# Revit family: Steni - Panel - Nature Type C
name_source: partatom
category: Generic Models
revit_build: Autodesk Revit Architecture 2014 (Build: 20131024_2115(x64)
units: mm (PartAtom-declared; Revit-internal decimal feet)

## types (3) — shared parameters
Allowable Variation = ± 2 mm
BIMobject Category = Cladding
BIMobject QR code url = http://steni.bimobject.com
Density = Apprx. 2000 Kg/m³
Design country = Norway
Diagonal Deviation = 3 mm
Drilling Distance Tolerance = ± 5 mm
Edge Straightness Full Size = 1 mm
Edition number = 1
Elasticity Module = 5000 MPa
Flexural Strength = 40 MPa
Hardness Of Aggregate = SEE SPEC.
Heat Conductivity = 0.55 W/m°C
Heat Resistance = 0.0074 m²°C/W
Humidity Altered Dimension = 5.2 X 106 m/m x%RF
IFC Classification = Covering
Impact Strength = 20 KJ / m 2
Impermeability = 100%
Installation instructions = http://steni.com
Manufacturer = Steni
Manufacturer URL = www.steni.com
Manufacturer country = Norway
Model = Steni - Panel - Nature Type C
Name of the object = Steni - Panel - Nature Type C
No Damage = 300 CYCLE
NominalHeight = 1195
NominalWidth = 3500
Penetration Of Water Vapour = 3,3 X 10-12 Kg/m²sPa
Product certification = http://steni.co.uk
Product data url = http://steni.com
Product family = Steni Nature
Product group = Coarse
Riverse Side = PLANE
Size Of Aggregate Particle = 5-8mm
Standard Length = 3500 mm
Standard Width = 1195 mm
Technical description = http://steni.no
Temperature Expansion (-20° +65°) = 0.021 mm/m°C
Tensile Strength = 15 N/mm²
Thickness 2 = Apprx. 14 ,mm
Type Of Aggregate = SEE SPEC.
UNSPC Category = Siding and exterior wall materials
UNSPC code = 301518
URL = http://steni.bimobject.com
Uniclass 1.4 Code = L381
Uniclass 1.4 Description = Facades and roofs
Water Absorbtion After 28 days = <1.5 %
Weight Net (kg) = Apprx. 18 Kg/m²

## per-type parameters (varying)
| type | Material main | Product SKU |
| SN 140 | Steni - Nature SN140 | SN140 |
| SN 117 | Steni - Nature SN117 | SN117 |
| SN 100 | Steni - Nature SN100 | SN100 |

## geometry (parser evidence)
native form markers: Sweep x3
no freeform markers — native parametric forms only
